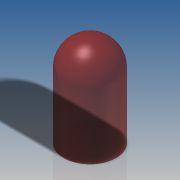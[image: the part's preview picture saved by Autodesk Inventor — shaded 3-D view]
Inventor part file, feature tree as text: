
AUTODESK INVENTOR PART (.ipt)
format: ipt  version: 2016 SP2 (Build 200236200, 236)  size: 109,056 bytes
history: native  units: in
note: dims shown in document units (in); Inventor stores cm internally (conversion verified against a paired STEP export)
features: revolve x1, sketch x1
ambient origin geometry x8: Origin, YZ Plane, XZ Plane, XY Plane, X Axis, Y Axis, Z Axis, Center Point
bodies: Solid1 (feature_tree)
feature tree (2):
  revolve  "Revolution1"  [1 undecoded]
  sketch  "Sketch2"  dims[d0=0.126in d1=0.2205in d2=90.0deg]
note: 1 required parameter value undecoded (feature->parameter linkage not recoverable at this tier; creation-order binding heuristic only, values carry confidence <= 0.55)
